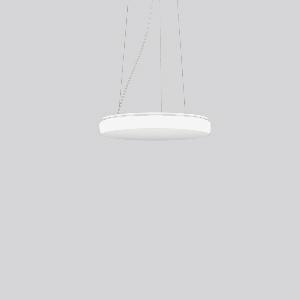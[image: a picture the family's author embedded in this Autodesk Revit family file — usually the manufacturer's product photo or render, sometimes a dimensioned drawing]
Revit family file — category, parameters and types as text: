
# Revit family: flat_polymero_kreis_slim_312090_002_4_5410
name_source: partatom
category: Lighting Fixtures
units: mm (PartAtom-declared; Revit-internal decimal feet)

## family parameters
Cut with Voids When Loaded = No
Host = Face
Light Source = No
Part Type = Normal
Room Calculation Point = No
Round Connector Dimension = Use Diameter
Shared = No

## types (1)
- FLAT POLYMERO KREIS SLIM (1 x LED Modul 840, 2100 lm, 4000)
    Apparent Load = 19 VA
    CIE Flux Codes = 44 75 94 92 100
    Color Rendering = 80
    Color Temperature = 4000
    Default Elevation = 1800 mm
    Description = Series: FLAT POLYMERO KREIS SLIM
Decorative round LED pendant luminaire. Base and canopy: metal, powder-coated, white. Canopy Ø 205 mm, h 35 mm. Diffuser made of plastic (polycarbonate), opal, shockproof. Diffuser fastening: patented push system. Homogeneous and smooth light distribution. Suitable for pendant. 3-point steel cable suspension, steplessly adjustable. Special lengths available on request. 
Colour: white
Diameter: 460 mm
Height: 68 mm
Suspension length: 200-1300 mm
Lamp: LED
Socket: without socket
Colour temperature: 4000K
Colour rendering index (CRI): 83
System power: 19 W
Rated luminous flux: 2100 lm
Luminous efficiency: 111 lm/W
Control gear: AC Strom, dim.Ph.an-/abschnitt
Protection class: I
Type of protection: IP 40
    Height = 68 mm
    Lamp = 1 x LED Modul 840
    Lamp Light Flux = 2100 lm
    Lamp count = 1
    Length = 460 mm
    Lifetime = 50000 h
    Luminous efficacy = 111 lm/W
    Manufacturer = RZB
    ModVariant = No
    Model = 312090.002.4
    Mounting Place = Ceiling
    Mounting Type = Pendant
    Number of Poles = 1
    OnlyDefault = Yes
    Power Factor = 1
    Product Name = FLAT POLYMERO KREIS SLIM
    Product group = Pendant luminaires
    ProductGroupID = 902
    Protection Class = Protection class I
    Protection Degree = IP 40
    RLX_Detail_Level = 1
    RLX_Emergency_Light_Flux = 0 lm
    RLX_Emergency_Type = 0
    RLX_Emergency_Type_DB = No
    RlxData = <blob elided: 57805 chars, md5=1c0dbc47>
    Socket = socket
    Standby Power = 0 W
    System Light Flux = 2100 lm
    System Power = 19 W
    Type Comments = Product without accessories
    Type Image = 312090.002.jpg
    URL = http://relux.com
    VarID = ---
    Voltage = 230 V
    Voltage Range = 220-240 V
    Weight = 0.00 kg
    Width = 0 mm  [stored 0 ft]

note: [stored X ft] marks values corroborated as IEEE doubles in the binary element streams (Revit-internal decimal feet)

## geometry (parser evidence)
native form markers: Blend x4, Sweep x12
no freeform markers — native parametric forms only
